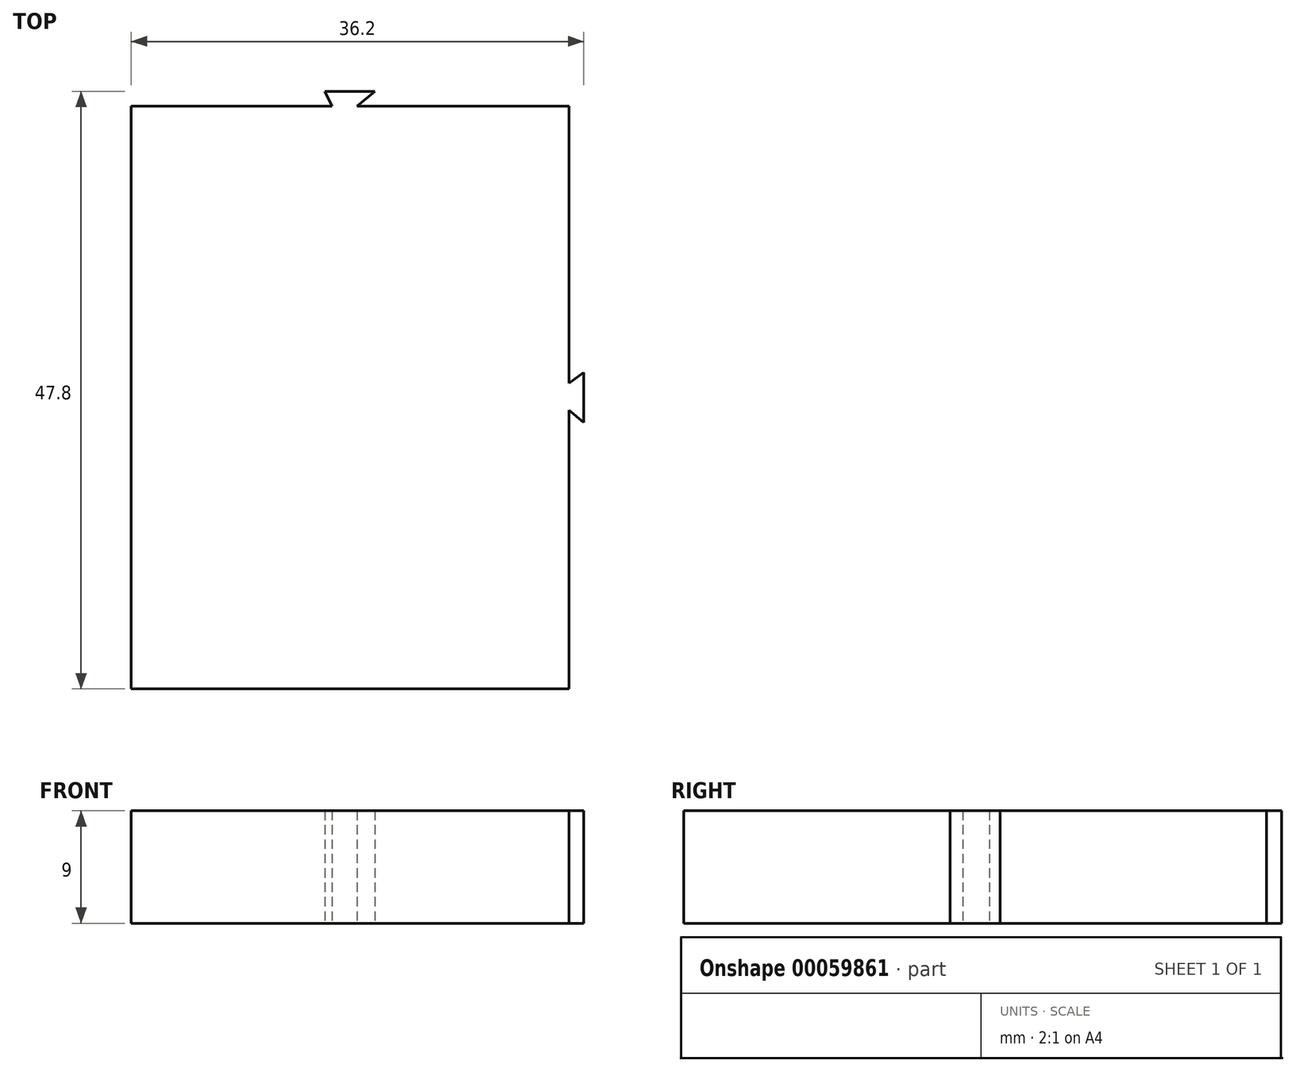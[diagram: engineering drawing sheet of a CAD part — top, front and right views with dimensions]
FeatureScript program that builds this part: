
annotation { "Feature Type Name" : "Feature", "Feature Type Description" : "" }
export const myFeature = defineFeature(function(context is Context, id is Id, definition is map)
    precondition{}
    {
        {
            var Q0;
            Q0=qCreatedBy(makeId("Top.planeOp"),FACE);
            var sketch = newSketch(context, id + "F0", { "sketchPlane" : qUnion([Q0])});
            skLineSegment(sketch, "E0.bottom", {"start": v(-25, 15) * mm, "end": v(25, 15) * mm});
            skLineSegment(sketch, "E0.top", {"start": v(-25, -15) * mm, "end": v(25, -15) * mm});
            skLineSegment(sketch, "E0.left", {"start": v(-25, 15) * mm, "end": v(-25, -15) * mm});
            skLineSegment(sketch, "E0.right", {"start": v(25, 15) * mm, "end": v(25, -15) * mm});
            skSolve(sketch);
        }
        {
            var Q0;
            Q0=makeQuery(id+"F0.imprint","IMPRINT",FACE,{"disambiguationData":[TD([[makeQuery(id+"F0.imprint","IMPRINT",EDGE,{"derivedFrom":sQuery(id+"F0.wireOp",EDGE,"E0.bottom")}),-1.0]])]});
            extrude(context, id + "F1", {"entities" : qUnion([Q0]), "depth" : 25 * mm});
        }
        {
            var Q0;
            Q0=makeQuery(id+"F1.opExtrude","SWEPT_FACE",FACE,{"disambiguationData":[OSD([sQuery(id+"F0.wireOp",EDGE,"E0.right")])]});
            var sketch = newSketch(context, id + "F2", { "sketchPlane" : qUnion([Q0])});
            skLineSegment(sketch, "E1", {"start": v(-15, 25) * mm, "end": v(-33.74, 0) * mm});
            skLineSegment(sketch, "E2", {"start": v(-33.74, 0) * mm, "end": v(-15, 0) * mm});
            skSolve(sketch);
        }
        {
            var Q0;
            Q0=makeQuery(id+"F2.imprint","IMPRINT",FACE,{"disambiguationData":[TD([[makeQuery(id+"F2.imprint","IMPRINT",EDGE,{"derivedFrom":sQuery(id+"F2.wireOp",EDGE,"E1")}),1.0]])]});
            var Q1;
            Q1=makeQuery(id+"F1.opExtrude","SWEPT_FACE",FACE,{"disambiguationData":[OSD([sQuery(id+"F0.wireOp",EDGE,"E0.left")])]});
            extrude(context, id + "F3", {"entities" : qUnion([Q0]), "endBound" : BoundingType.UP_TO_SURFACE, "oppositeDirection" : true, "endBoundEntityFace" : qUnion([Q1]), "depth" : 25 * mm});
        }
        {
            var Q0;
            Q0=makeQuery(id+"F1.opExtrude","SWEPT_BODY",BODY,{"disambiguationData":[OSD([sQuery(id+"F0.wireOp",EDGE,"E0.bottom"),sQuery(id+"F0.wireOp",EDGE,"E0.top"),sQuery(id+"F0.wireOp",EDGE,"E0.left"),sQuery(id+"F0.wireOp",EDGE,"E0.right")])]});
            var Q1;
            Q1=makeQuery(id+"F3.opExtrude","SWEPT_BODY",BODY,{"disambiguationData":[OSD([sQuery(id+"F0.wireOp",EDGE,"E0.top"),sQuery(id+"F0.wireOp",EDGE,"E0.right"),sQuery(id+"F2.wireOp",EDGE,"E1"),sQuery(id+"F2.wireOp",EDGE,"E2")])]});
            booleanBodies(context, id + "F4", {"operationType" : BooleanOperationType.UNION, "tools" : qUnion([Q0, Q1])});
        }
        {
            var Q0;
            Q0=makeQuery(id+"F3.opExtrude","CAP_EDGE",EDGE,{"disambiguationData":[OSD([sQuery(id+"F2.wireOp",EDGE,"E1")])],"isStart":true});
            var Q1;
            Q1=makeQuery(id+"F3.opExtrude","CAP_EDGE",EDGE,{"disambiguationData":[OSD([sQuery(id+"F2.wireOp",EDGE,"E1")])],"isStart":false});
            var Q2;
            {var subQ0=sQuery(id+"F0.wireOp",EDGE,"E0.top");Q2=makeQuery(id+"F4.opBoolean","MERGE",EDGE,{"derivedFrom":[makeQuery(id+"F1.opExtrude","CAP_EDGE",EDGE,{"disambiguationData":[OSD([subQ0])],"isStart":false}),makeQuery(id+"F3.opExtrude","SWEPT_EDGE",EDGE,{"disambiguationData":[OSD([subQ0,sQuery(id+"F0.wireOp",EDGE,"E0.right"),sQuery(id+"F2.wireOp",EDGE,"E1")])]})]});}
            var Q3;
            Q3=makeQuery(id+"F1.opExtrude","CAP_EDGE",EDGE,{"disambiguationData":[OSD([sQuery(id+"F0.wireOp",EDGE,"E0.right")])],"isStart":false});
            var Q4;
            Q4=makeQuery(id+"F1.opExtrude","CAP_EDGE",EDGE,{"disambiguationData":[OSD([sQuery(id+"F0.wireOp",EDGE,"E0.left")])],"isStart":false});
            fillet(context, id + "F5", {"entities" : qUnion([Q0, Q1, Q2, Q3, Q4]), "radius" : 5 * mm, "tangentPropagation" : true, "allowEdgeOverflow" : false});
        }
        {
            var Q0;
            Q0=makeQuery(id+"F4.opBoolean","MERGE",FACE,{"derivedFrom":[makeQuery(id+"F1.opExtrude","CAP_FACE",FACE,{"disambiguationData":[OSD([sQuery(id+"F0.wireOp",EDGE,"E0.bottom"),sQuery(id+"F0.wireOp",EDGE,"E0.top"),sQuery(id+"F0.wireOp",EDGE,"E0.left"),sQuery(id+"F0.wireOp",EDGE,"E0.right")])],"isStart":true}),makeQuery(id+"F3.opExtrude","SWEPT_FACE",FACE,{"disambiguationData":[OSD([sQuery(id+"F2.wireOp",EDGE,"E2")])]})]});
            shell(context, id + "F6", {"entities" : qUnion([Q0]), "thickness" : 2.5 * mm});
        }
        {
            var Q0;
            Q0=makeQuery(id+"F3.opExtrude","SWEPT_FACE",FACE,{"disambiguationData":[OSD([sQuery(id+"F2.wireOp",EDGE,"E1")])]});
            var sketch = newSketch(context, id + "F7", { "sketchPlane" : qUnion([Q0])});
            skCircle(sketch, "E3", {"center": v(0, -5.5) * mm, "radius": 10.8 * mm});
            skSolve(sketch);
        }
        {
            var Q0;
            Q0=qSketchRegion(id+"F7",true);
            extrude(context, id + "F8", {"entities" : qUnion([Q0]), "operationType" : NewBodyOperationType.REMOVE, "oppositeDirection" : true, "depth" : 25 * mm});
        }
        {
            var Q0;
            Q0=qCreatedBy(makeId("Top.planeOp"),FACE);
            var sketch = newSketch(context, id + "F9", { "sketchPlane" : qUnion([Q0])});
            skLineSegment(sketch, "E4.bottom", {"start": v(-17.5, 22) * mm, "end": v(17.5, 22) * mm});
            skLineSegment(sketch, "E4.top", {"start": v(-17.5, 68.6) * mm, "end": v(17.5, 68.6) * mm});
            skLineSegment(sketch, "E4.left", {"start": v(-17.5, 22) * mm, "end": v(-17.5, 68.6) * mm});
            skLineSegment(sketch, "E4.right", {"start": v(17.5, 22) * mm, "end": v(17.5, 68.6) * mm});
            skLineSegment(sketch, "E5", {"start": v(22.18, 45.3) * mm, "end": v(-29.67, 45.3) * mm, "construction": true});
            skLineSegment(sketch, "E6", {"start": v(17.5, 44.3) * mm, "end": v(18.7, 43.3) * mm});
            skLineSegment(sketch, "E7", {"start": v(18.7, 43.3) * mm, "end": v(18.7, 47.3) * mm});
            skLineSegment(sketch, "E8", {"start": v(18.7, 47.3) * mm, "end": v(17.5, 46.45) * mm});
            skLineSegment(sketch, "E9", {"start": v(0, 19.5) * mm, "end": v(0, 72.59) * mm, "construction": true});
            skLineSegment(sketch, "E10", {"start": v(2, 69.8) * mm, "end": v(-2, 69.8) * mm});
            skLineSegment(sketch, "E11", {"start": v(2, 69.8) * mm, "end": v(0.55, 68.6) * mm});
            skLineSegment(sketch, "E12", {"start": v(-2, 69.8) * mm, "end": v(-1.45, 68.6) * mm});
            skSolve(sketch);
        }
        {
            var Q0;
            Q0=qSketchRegion(id+"F9",true);
            extrude(context, id + "F10", {"entities" : qUnion([Q0]), "depth" : 9 * mm});
        }
        {
            var Q0;
            Q0=qCreatedBy(makeId("Top.planeOp"),FACE);
            var sketch = newSketch(context, id + "F11", { "sketchPlane" : qUnion([Q0])});
            skLineSegment(sketch, "E13.bottom", {"start": v(21, 0) * mm, "end": v(-21, 0) * mm});
            skLineSegment(sketch, "E13.top", {"start": v(21, 73.17) * mm, "end": v(-21, 73.17) * mm});
            skLineSegment(sketch, "E13.left", {"start": v(21, 0) * mm, "end": v(21, 73.17) * mm});
            skLineSegment(sketch, "E13.right", {"start": v(-21, 0) * mm, "end": v(-21, 73.17) * mm});
            skSolve(sketch);
        }
        {
            var Q0;
            Q0=qSketchRegion(id+"F11",true);
            var Q1;
            Q1=makeQuery(id+"F6.opShell","OFFSET_FACE",FACE,{"disambiguationData":[OSD([sQuery(id+"F0.wireOp",EDGE,"E0.bottom"),sQuery(id+"F0.wireOp",EDGE,"E0.top"),sQuery(id+"F0.wireOp",EDGE,"E0.left"),sQuery(id+"F0.wireOp",EDGE,"E0.right")])]});
            extrude(context, id + "F12", {"entities" : qUnion([Q0]), "endBound" : BoundingType.UP_TO_SURFACE, "endBoundEntityFace" : qUnion([Q1]), "depth" : 18 * mm});
        }
        {
            var Q0;
            Q0=makeQuery(id+"F12.opExtrude","SWEPT_BODY",BODY,{"disambiguationData":[OSD([sQuery(id+"F11.wireOp",EDGE,"E13.bottom"),sQuery(id+"F11.wireOp",EDGE,"E13.top"),sQuery(id+"F11.wireOp",EDGE,"E13.left"),sQuery(id+"F11.wireOp",EDGE,"E13.right")])]});
            var Q1;
            Q1=makeQuery(id+"F1.opExtrude","SWEPT_BODY",BODY,{"disambiguationData":[OSD([sQuery(id+"F0.wireOp",EDGE,"E0.bottom"),sQuery(id+"F0.wireOp",EDGE,"E0.top"),sQuery(id+"F0.wireOp",EDGE,"E0.left"),sQuery(id+"F0.wireOp",EDGE,"E0.right")])]});
            booleanBodies(context, id + "F13", {"operationType" : BooleanOperationType.SUBTRACTION, "tools" : qUnion([Q0]), "targets" : qUnion([Q1])});
        }
        {
            var Q0;
            Q0=makeQuery(id+"F1.opExtrude","SWEPT_BODY",BODY,{"disambiguationData":[OSD([sQuery(id+"F0.wireOp",EDGE,"E0.bottom"),sQuery(id+"F0.wireOp",EDGE,"E0.top"),sQuery(id+"F0.wireOp",EDGE,"E0.left"),sQuery(id+"F0.wireOp",EDGE,"E0.right")])]});
            transform(context, id + "F14", {"entities" : qUnion([Q0]), "transformType" : TransformType.TRANSLATION_3D, "dx" : 0 * mm, "dy" : 0 * mm, "dz" : 0 * mm, "makeCopy" : true});
        }
        {
            var Q0;
            Q0=makeQuery(id+"F1.opExtrude","SWEPT_BODY",BODY,{"disambiguationData":[OSD([sQuery(id+"F0.wireOp",EDGE,"E0.bottom"),sQuery(id+"F0.wireOp",EDGE,"E0.top"),sQuery(id+"F0.wireOp",EDGE,"E0.left"),sQuery(id+"F0.wireOp",EDGE,"E0.right")])]});
            deleteBodies(context, id + "F15", {"entities" : qUnion([Q0])});
        }
        {
            var Q0;
            Q0=makeQuery(id+"F14.opPattern","COPY",BODY,{"derivedFrom":makeQuery(id+"F1.opExtrude","SWEPT_BODY",BODY,{"disambiguationData":[OSD([sQuery(id+"F0.wireOp",EDGE,"E0.bottom"),sQuery(id+"F0.wireOp",EDGE,"E0.top"),sQuery(id+"F0.wireOp",EDGE,"E0.left"),sQuery(id+"F0.wireOp",EDGE,"E0.right")])]}),"instanceName":"1"});
            deleteBodies(context, id + "F16", {"entities" : qUnion([Q0])});
        }
    });
